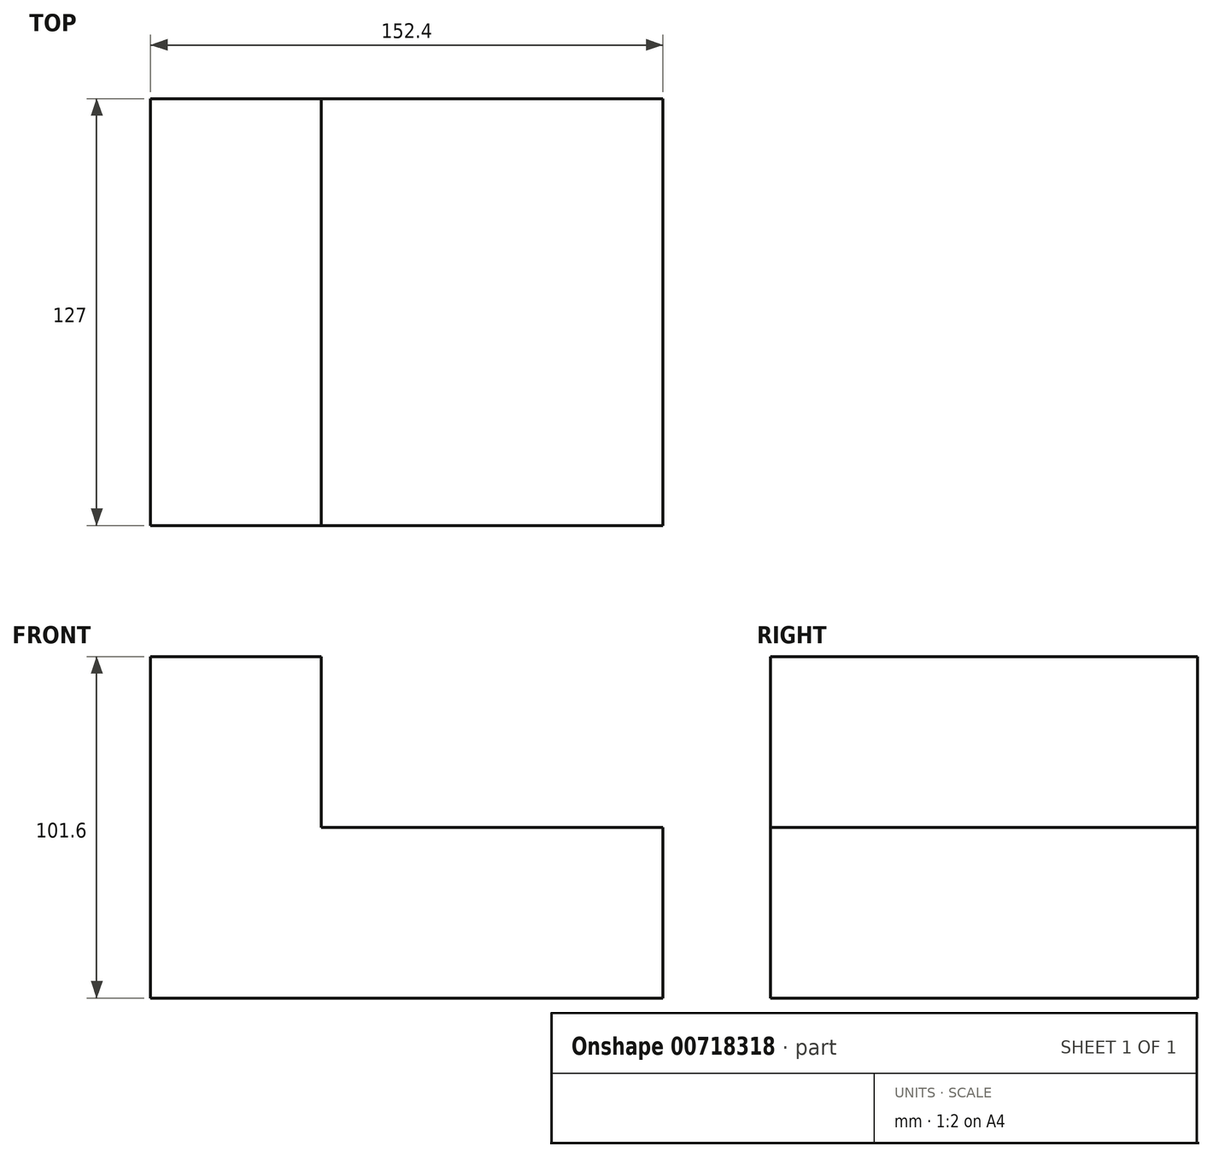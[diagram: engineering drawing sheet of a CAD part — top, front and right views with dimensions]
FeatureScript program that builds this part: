
annotation { "Feature Type Name" : "Feature", "Feature Type Description" : "" }
export const myFeature = defineFeature(function(context is Context, id is Id, definition is map)
    precondition{}
    {
        {
            var Q0;
            Q0=qCreatedBy(makeId("Front.planeOp"),FACE);
            var sketch = newSketch(context, id + "F0", { "sketchPlane" : qUnion([Q0])});
            skLineSegment(sketch, "E0", {"start": v(-76.43, -68.15) * mm, "end": v(75.97, -68.15) * mm});
            skLineSegment(sketch, "E1", {"start": v(75.97, -68.15) * mm, "end": v(75.97, -17.35) * mm});
            skLineSegment(sketch, "E2", {"start": v(75.97, -17.35) * mm, "end": v(-25.63, -17.35) * mm});
            skLineSegment(sketch, "E3", {"start": v(-25.63, -17.35) * mm, "end": v(-25.63, 33.45) * mm});
            skLineSegment(sketch, "E4", {"start": v(-25.63, 33.45) * mm, "end": v(-76.43, 33.45) * mm});
            skLineSegment(sketch, "E5", {"start": v(-76.43, 33.45) * mm, "end": v(-76.43, -68.15) * mm});
            skSolve(sketch);
        }
        {
            var Q0;
            Q0=makeQuery(id+"F0.imprint","IMPRINT",FACE,{"disambiguationData":[TD([[makeQuery(id+"F0.imprint","IMPRINT",EDGE,{"derivedFrom":sQuery(id+"F0.wireOp",EDGE,"E0")}),1.0]])]});
            extrude(context, id + "F1", {"entities" : qUnion([Q0]), "depth" : 127 * mm, "offsetDistance" : 25.4 * mm});
        }
    });
